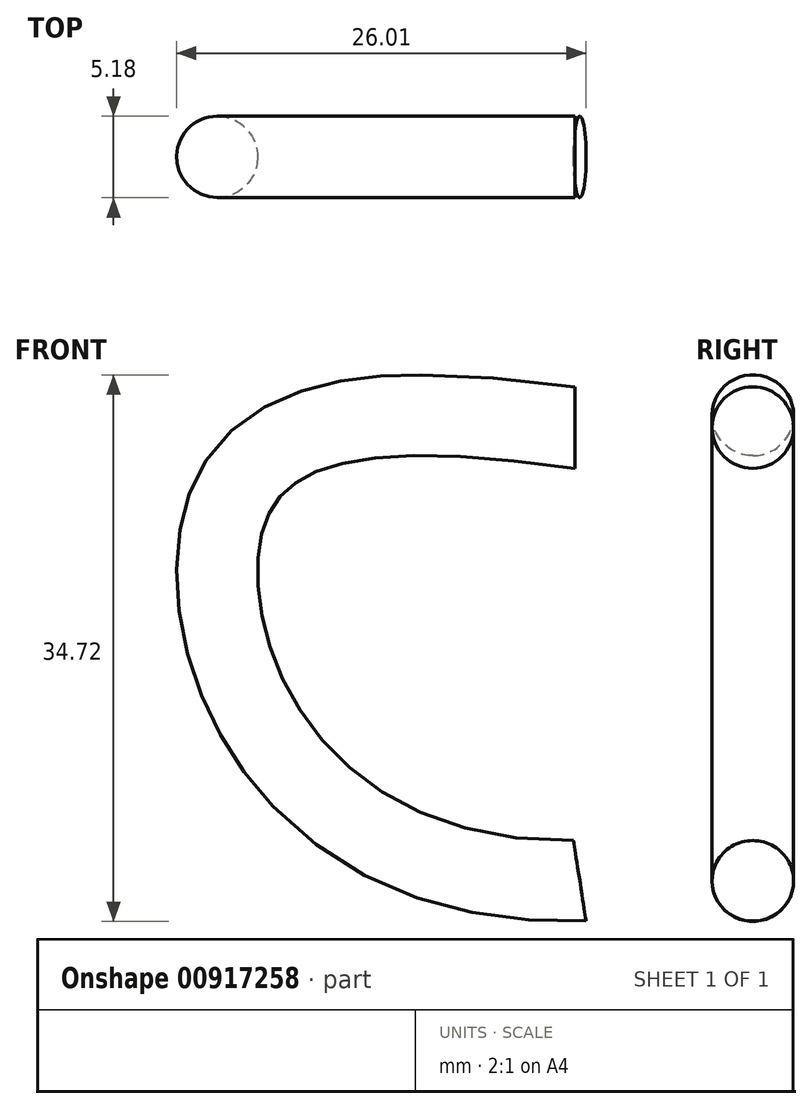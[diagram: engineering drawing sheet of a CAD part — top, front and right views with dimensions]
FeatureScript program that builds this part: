
annotation { "Feature Type Name" : "Feature", "Feature Type Description" : "" }
export const myFeature = defineFeature(function(context is Context, id is Id, definition is map)
    precondition{}
    {
        {
            var Q0;
            Q0=qCreatedBy(makeId("Front.planeOp"),FACE);
            var sketch = newSketch(context, id + "F0", { "sketchPlane" : qUnion([Q0])});
            skFitSpline(sketch, "E0", {"points": [v(0, 5.96) * mm, v(-20.75, 0) * mm, v(0, -18.98) * mm], "startDerivative": vector(-95.63, 13.35) * mm, "endDerivative": vector(91.1, 1.48) * mm});
            skSolve(sketch);
        }
        {
            var Q0;
            Q0=qCreatedBy(makeId("Right.planeOp"),FACE);
            var sketch = newSketch(context, id + "F1", { "sketchPlane" : qUnion([Q0])});
            skCircle(sketch, "E1", {"center": v(0, 7.9) * mm, "radius": 2.59 * mm});
            skSolve(sketch);
        }
        {
            var Q0;
            Q0=makeQuery(id+"F1.imprint","IMPRINT",FACE,{"disambiguationData":[TD([[makeQuery(id+"F1.imprint","IMPRINT",EDGE,{"derivedFrom":sQuery(id+"F1.wireOp",EDGE,"E1")}),1.0]])]});
            var Q1;
            Q1=sQuery(id+"F0.wireOp",EDGE,"E0");
            sweep(context, id + "F2", {"profiles" : qUnion([Q0]), "path" : qUnion([Q1])});
        }
    });
